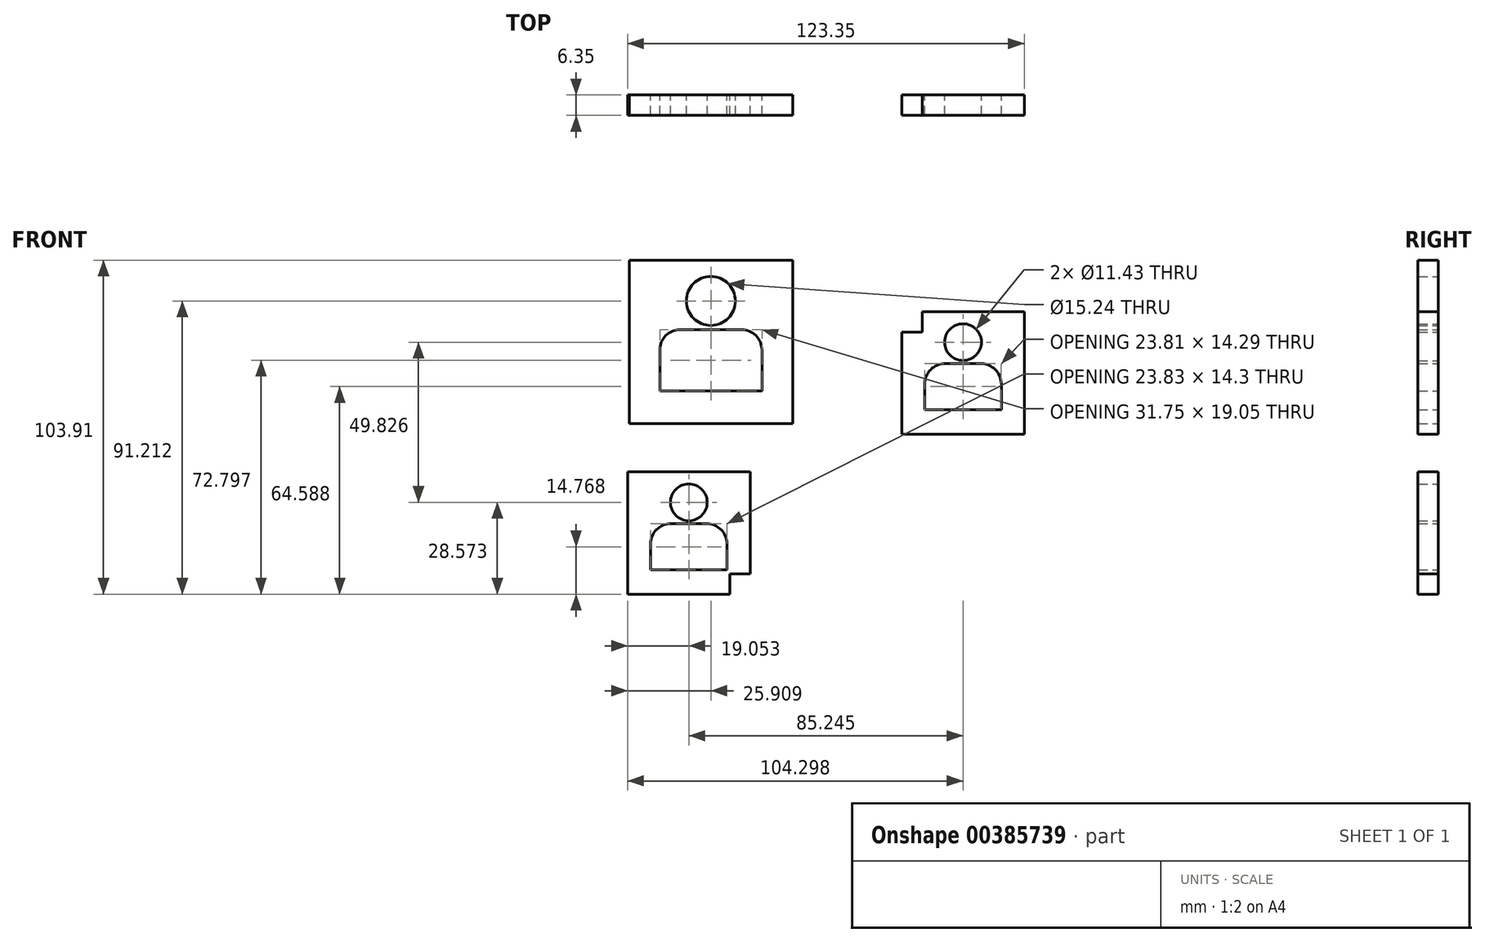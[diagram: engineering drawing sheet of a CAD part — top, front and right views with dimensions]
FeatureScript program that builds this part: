
annotation { "Feature Type Name" : "Feature", "Feature Type Description" : "" }
export const myFeature = defineFeature(function(context is Context, id is Id, definition is map)
    precondition{}
    {
        {
            var Q0;
            Q0=qCreatedBy(makeId("Front.planeOp"),FACE);
            var sketch = newSketch(context, id + "F0", { "sketchPlane" : qUnion([Q0])});
            skLineSegment(sketch, "E0.bottom", {"start": v(-58, 60.05) * mm, "end": v(-7.2, 60.05) * mm});
            skLineSegment(sketch, "E0.top", {"start": v(-58, 9.25) * mm, "end": v(-7.2, 9.25) * mm});
            skLineSegment(sketch, "E0.left", {"start": v(-58, 60.05) * mm, "end": v(-58, 9.25) * mm});
            skLineSegment(sketch, "E0.right", {"start": v(-7.2, 60.05) * mm, "end": v(-7.2, 9.25) * mm});
            skCircle(sketch, "E1", {"center": v(-32.6, 47.35) * mm, "radius": 7.62 * mm});
            skLineSegment(sketch, "E2.bottom", {"start": v(-42.12, 38.46) * mm, "end": v(-23.07, 38.46) * mm});
            skLineSegment(sketch, "E2.top", {"start": v(-48.47, 19.41) * mm, "end": v(-16.72, 19.41) * mm});
            skLineSegment(sketch, "E2.left", {"start": v(-48.47, 32.11) * mm, "end": v(-48.47, 19.41) * mm});
            skLineSegment(sketch, "E2.right", {"start": v(-16.72, 32.11) * mm, "end": v(-16.72, 19.41) * mm});
            skLineSegment(sketch, "E3", {"start": v(-32.6, 9.25) * mm, "end": v(-32.6, 19.41) * mm, "construction": true});
            skLineSegment(sketch, "E4", {"start": v(-32.6, 47.35) * mm, "end": v(-32.6, 60.05) * mm, "construction": true});
            skLineSegment(sketch, "E5", {"start": v(-48.47, 28.94) * mm, "end": v(-58, 28.94) * mm, "construction": true});
            skLineSegment(sketch, "E6", {"start": v(-51.64, 60.05) * mm, "end": v(-51.64, 53.7) * mm, "construction": true});
            skLineSegment(sketch, "E7", {"start": v(-51.64, 53.7) * mm, "end": v(-58, 53.7) * mm, "construction": true});
            skLineSegment(sketch, "E8", {"start": v(-13.54, 9.25) * mm, "end": v(-13.54, 15.6) * mm, "construction": true});
            skLineSegment(sketch, "E9", {"start": v(-13.54, 15.6) * mm, "end": v(-7.2, 15.6) * mm, "construction": true});
            skPoint(sketch, "E10.visualSharp", {"position": v(-48.47, 38.46) * mm});
            skArc(sketch, "E10.filletArc", {"start": v(-42.12, 38.46) * mm, "mid": v(-46.6, 36.6) * mm, "end": v(-48.47, 32.11) * mm});
            skPoint(sketch, "E11.visualSharp", {"position": v(-16.72, 38.46) * mm});
            skArc(sketch, "E11.filletArc", {"start": v(-16.72, 32.11) * mm, "mid": v(-18.58, 36.6) * mm, "end": v(-23.07, 38.46) * mm});
            skSolve(sketch);
        }
        {
            var Q0;
            Q0=qCreatedBy(makeId("Front.planeOp"),FACE);
            var sketch = newSketch(context, id + "F1", { "sketchPlane" : qUnion([Q0])});
            skLineSegment(sketch, "E12.bottom", {"start": v(26.75, 44.06) * mm, "end": v(64.85, 44.06) * mm});
            skLineSegment(sketch, "E12.top", {"start": v(26.75, 5.96) * mm, "end": v(64.85, 5.96) * mm});
            skLineSegment(sketch, "E12.left", {"start": v(26.75, 44.06) * mm, "end": v(26.75, 5.96) * mm});
            skLineSegment(sketch, "E12.right", {"start": v(64.85, 44.06) * mm, "end": v(64.85, 5.96) * mm});
            skLineSegment(sketch, "E13.bottom", {"start": v(40.24, 27.87) * mm, "end": v(51.35, 27.87) * mm});
            skLineSegment(sketch, "E13.top", {"start": v(33.9, 13.58) * mm, "end": v(57.7, 13.58) * mm});
            skLineSegment(sketch, "E13.left", {"start": v(33.9, 21.52) * mm, "end": v(33.9, 13.58) * mm});
            skLineSegment(sketch, "E13.right", {"start": v(57.7, 21.52) * mm, "end": v(57.7, 13.58) * mm});
            skLineSegment(sketch, "E14", {"start": v(26.75, 37.71) * mm, "end": v(33.1, 37.71) * mm});
            skLineSegment(sketch, "E15", {"start": v(33.1, 37.71) * mm, "end": v(33.1, 44.06) * mm});
            skCircle(sketch, "E16", {"center": v(45.8, 34.54) * mm, "radius": 5.72 * mm});
            skLineSegment(sketch, "E17", {"start": v(45.8, 44.06) * mm, "end": v(45.8, 34.54) * mm, "construction": true});
            skLineSegment(sketch, "E18", {"start": v(45.8, 5.96) * mm, "end": v(45.8, 13.58) * mm, "construction": true});
            skPoint(sketch, "E19.visualSharp", {"position": v(33.9, 27.87) * mm});
            skArc(sketch, "E19.filletArc", {"start": v(40.24, 27.87) * mm, "mid": v(35.75, 26.01) * mm, "end": v(33.9, 21.52) * mm});
            skPoint(sketch, "E20.visualSharp", {"position": v(57.7, 27.87) * mm});
            skArc(sketch, "E20.filletArc", {"start": v(57.7, 21.52) * mm, "mid": v(55.84, 26.01) * mm, "end": v(51.35, 27.87) * mm});
            skSolve(sketch);
        }
        {
            var Q0;
            Q0=qCreatedBy(makeId("Front.planeOp"),FACE);
            var sketch = newSketch(context, id + "F2", { "sketchPlane" : qUnion([Q0])});
            skLineSegment(sketch, "E21.bottom", {"start": v(-58.5, -5.76) * mm, "end": v(-20.4, -5.76) * mm});
            skLineSegment(sketch, "E21.top", {"start": v(-58.5, -43.86) * mm, "end": v(-20.4, -43.86) * mm});
            skLineSegment(sketch, "E21.left", {"start": v(-58.5, -5.76) * mm, "end": v(-58.5, -43.86) * mm});
            skLineSegment(sketch, "E21.right", {"start": v(-20.4, -5.76) * mm, "end": v(-20.4, -43.86) * mm});
            skLineSegment(sketch, "E22.bottom", {"start": v(-45, -21.94) * mm, "end": v(-33.88, -21.94) * mm});
            skLineSegment(sketch, "E22.top", {"start": v(-51.36, -36.24) * mm, "end": v(-27.53, -36.24) * mm});
            skLineSegment(sketch, "E22.left", {"start": v(-51.36, -28.3) * mm, "end": v(-51.36, -36.24) * mm});
            skLineSegment(sketch, "E22.right", {"start": v(-27.53, -28.3) * mm, "end": v(-27.53, -36.24) * mm});
            skCircle(sketch, "E23", {"center": v(-39.45, -15.29) * mm, "radius": 5.72 * mm});
            skLineSegment(sketch, "E24", {"start": v(-39.45, -5.76) * mm, "end": v(-39.45, -15.29) * mm, "construction": true});
            skLineSegment(sketch, "E25", {"start": v(-39.45, -43.86) * mm, "end": v(-39.45, -36.24) * mm, "construction": true});
            skLineSegment(sketch, "E26", {"start": v(-26.75, -43.86) * mm, "end": v(-26.75, -37.51) * mm});
            skLineSegment(sketch, "E27", {"start": v(-26.75, -37.51) * mm, "end": v(-20.4, -37.51) * mm});
            skPoint(sketch, "E28.visualSharp", {"position": v(-51.36, -21.94) * mm});
            skArc(sketch, "E28.filletArc", {"start": v(-45, -21.94) * mm, "mid": v(-49.5, -23.8) * mm, "end": v(-51.36, -28.3) * mm});
            skPoint(sketch, "E29.visualSharp", {"position": v(-27.53, -21.94) * mm});
            skArc(sketch, "E29.filletArc", {"start": v(-27.53, -28.3) * mm, "mid": v(-29.4, -23.8) * mm, "end": v(-33.88, -21.94) * mm});
            skSolve(sketch);
        }
        {
            var Q0;
            Q0=makeQuery(id+"F0.imprint","IMPRINT",FACE,{"disambiguationData":[TD([[makeQuery(id+"F0.imprint","IMPRINT",EDGE,{"derivedFrom":sQuery(id+"F0.wireOp",EDGE,"E0.bottom")}),-1.0]])]});
            extrude(context, id + "F3", {"entities" : qUnion([Q0]), "depth" : 6.35 * mm});
        }
        {
            var Q0;
            {var subQ4=sQuery(id+"F1.wireOp",EDGE,"E12.top");Q0=makeQuery(id+"F1.imprint","IMPRINT",FACE,{"disambiguationData":[TD([[makeQuery(id+"F1.imprint","IMPRINT",EDGE,{"derivedFrom":subQ4}),1.0]])]});}
            var Q1;
            {var subQ1=sQuery(id+"F2.wireOp",EDGE,"E21.bottom");Q1=makeQuery(id+"F2.imprint","IMPRINT",FACE,{"disambiguationData":[TD([[makeQuery(id+"F2.imprint","IMPRINT",EDGE,{"derivedFrom":subQ1}),-1.0]])]});}
            extrude(context, id + "F4", {"entities" : qUnion([Q0, Q1]), "depth" : 6.35 * mm});
        }
    });
